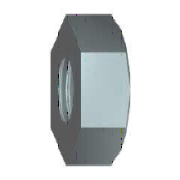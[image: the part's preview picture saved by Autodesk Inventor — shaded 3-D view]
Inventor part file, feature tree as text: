
AUTODESK INVENTOR PART (.ipt)
format: ipt  version: 2023 (Build 270158000, 158)  size: 165,888 bytes
history: native  units: mm
features: other x4, sketch x3, extrude x1, chamfer x1, revolve x1
ambient origin geometry x8: Origin, YZ Plane, XZ Plane, XY Plane, X Axis, Y Axis, Z Axis, Center Point
bodies: Solid1 (feature_tree)
feature tree (10):
  extrude  "Extrusion1"  Depth=5.1mm
  chamfer  "Chamfer1"  Distance=0.4mm
  revolve  "Revolution1"  Angle=45.0deg
  other  "MSC_A1"
  other  "MSC_PT1"
  other  "MSC_PT2"
  other  "MSC_PF1"
  sketch  "Sketch1"  dims[d0=8.0mm d1=5.1mm]
  sketch  "Sketch2"  dims[d2=0.0mm]
  sketch  "Sketch3"  dims[d3=4.134mm d4=6.0mm d5=4.0mm d6=2.0mm d7=90.0deg d8=8.0mm d9=20.594885mm d10=0.4mm d11=2.0mm d12=45.0deg d15=90.0deg d16=0.0mm d17=0.0mm d18=0.0mm d19=0.0mm d21=0.0mm d22=0.0mm d23=0.0mm d32=4.0mm d33=30.0deg]
